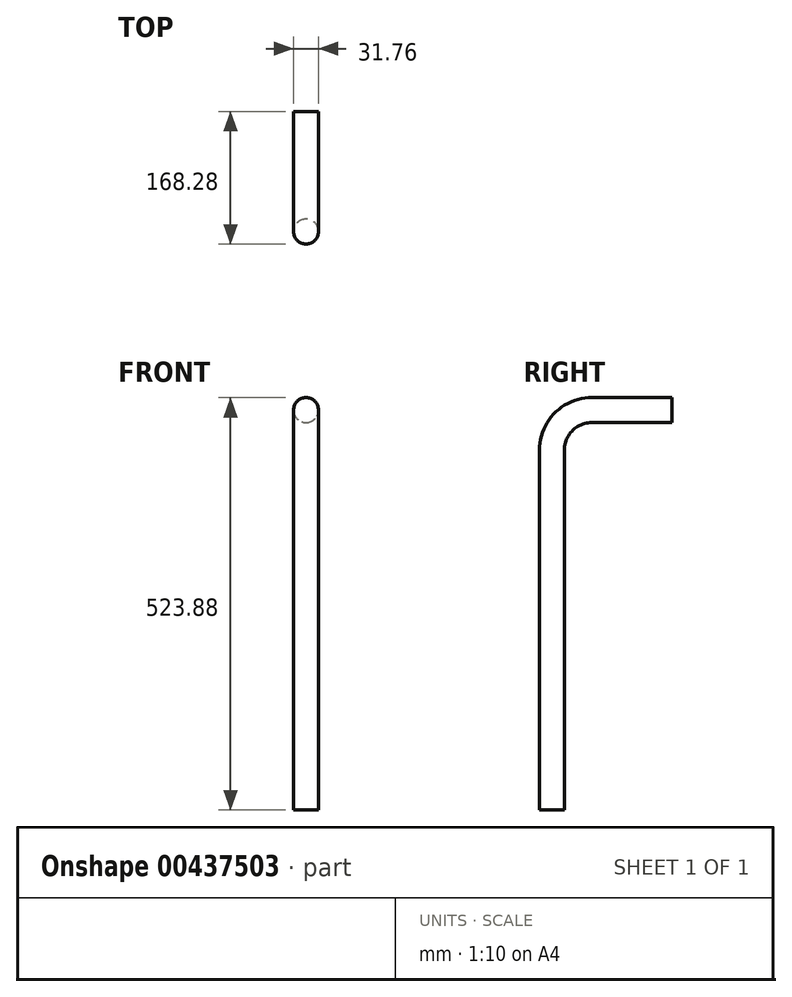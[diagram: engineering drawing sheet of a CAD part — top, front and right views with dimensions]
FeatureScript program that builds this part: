
annotation { "Feature Type Name" : "Feature", "Feature Type Description" : "" }
export const myFeature = defineFeature(function(context is Context, id is Id, definition is map)
    precondition{}
    {
        {
            var Q0;
            Q0=qCreatedBy(makeId("Right.planeOp"),FACE);
            var sketch = newSketch(context, id + "F0", { "sketchPlane" : qUnion([Q0])});
            skLineSegment(sketch, "E0", {"start": v(0, 0) * mm, "end": v(0, 457.2) * mm});
            skLineSegment(sketch, "E1", {"start": v(0, 457.2) * mm, "end": v(0, 457.2) * mm});
            skLineSegment(sketch, "E2", {"start": v(50.8, 508) * mm, "end": v(50.8, 508) * mm});
            skPoint(sketch, "E3.visualSharp", {"position": v(0, 508) * mm});
            skArc(sketch, "E3.filletArc", {"start": v(50.8, 508) * mm, "mid": v(14.88, 493.12) * mm, "end": v(0, 457.2) * mm});
            skLineSegment(sketch, "E4", {"start": v(50.8, 508) * mm, "end": v(152.4, 508) * mm});
            skSolve(sketch);
        }
        {
            var Q0;
            Q0=qCreatedBy(makeId("Top.planeOp"),FACE);
            var sketch = newSketch(context, id + "F1", { "sketchPlane" : qUnion([Q0])});
            skCircle(sketch, "E5", {"center": v(0, 0) * mm, "radius": 15.88 * mm});
            skSolve(sketch);
        }
        {
            var Q0;
            Q0=makeQuery(id+"F1.imprint","IMPRINT",FACE,{"disambiguationData":[TD([[makeQuery(id+"F1.imprint","IMPRINT",EDGE,{"derivedFrom":sQuery(id+"F1.wireOp",EDGE,"E5")}),1.0]])]});
            var Q1;
            Q1=sQuery(id+"F0.wireOp",EDGE,"E3.filletArc");
            var Q2;
            Q2=sQuery(id+"F0.wireOp",EDGE,"E4");
            var Q3;
            Q3=sQuery(id+"F0.wireOp",EDGE,"E0");
            sweep(context, id + "F2", {"profiles" : qUnion([Q0]), "path" : qUnion([Q1, Q2, Q3])});
        }
    });
